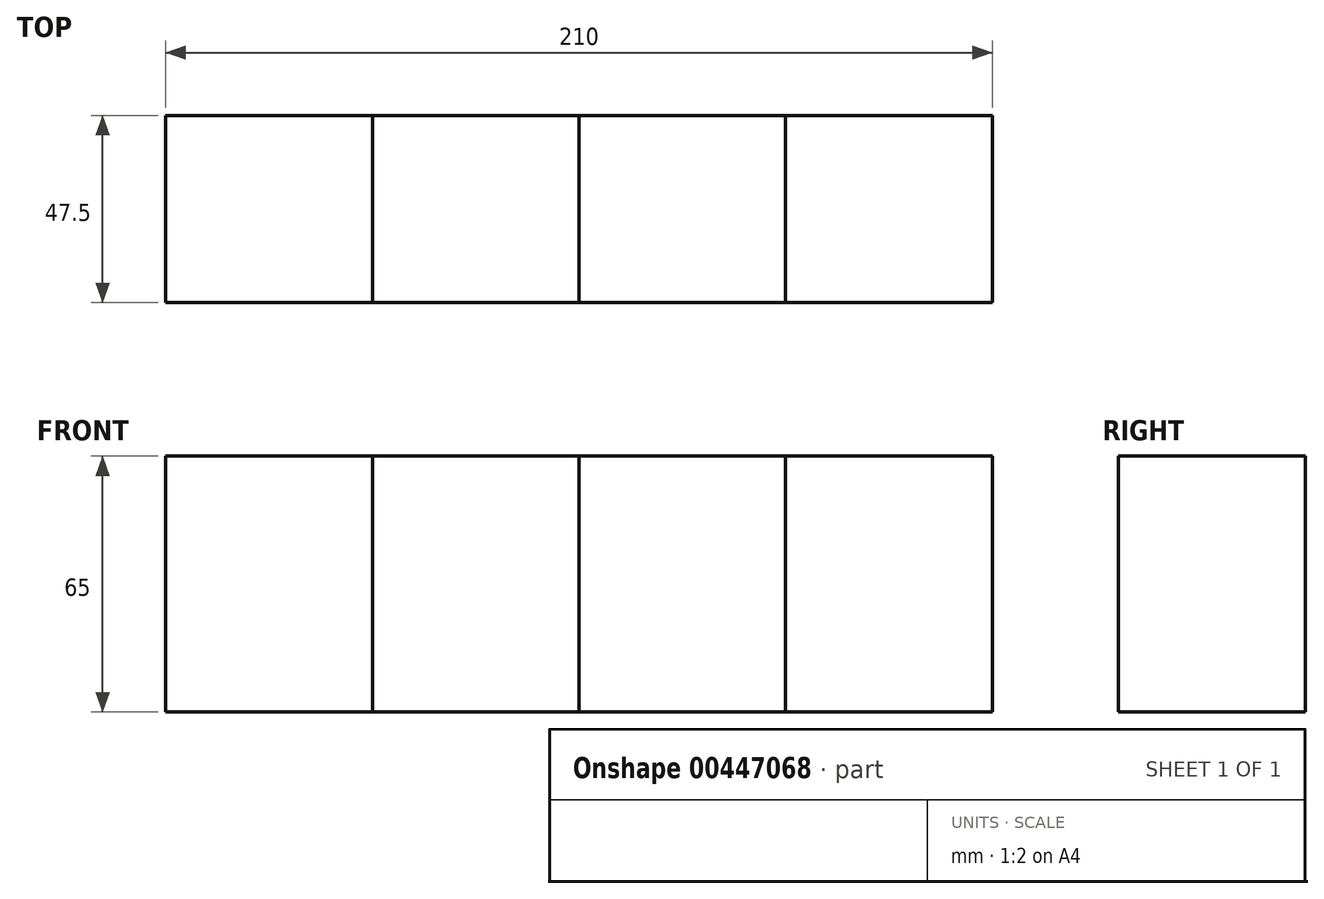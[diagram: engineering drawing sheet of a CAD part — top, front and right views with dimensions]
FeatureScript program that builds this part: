
annotation { "Feature Type Name" : "Feature", "Feature Type Description" : "" }
export const myFeature = defineFeature(function(context is Context, id is Id, definition is map)
    precondition{}
    {
        {
            var Q0;
            Q0=qCreatedBy(makeId("Right.planeOp"),FACE);
            var sketch = newSketch(context, id + "F0", { "sketchPlane" : qUnion([Q0])});
            skLineSegment(sketch, "E0.bottom", {"start": v(50, -32.5) * mm, "end": v(-50, -32.5) * mm});
            skLineSegment(sketch, "E0.top", {"start": v(50, 32.5) * mm, "end": v(-50, 32.5) * mm});
            skLineSegment(sketch, "E0.left", {"start": v(50, -32.5) * mm, "end": v(50, 32.5) * mm});
            skLineSegment(sketch, "E0.right", {"start": v(-50, -32.5) * mm, "end": v(-50, 32.5) * mm});
            skPoint(sketch, "E0.middle", {"position": v(0, 0) * mm});
            skLineSegment(sketch, "E1", {"start": v(2.5, -32.5) * mm, "end": v(2.5, 32.5) * mm});
            skSolve(sketch);
        }
        {
            var Q0;
            Q0=makeQuery(id+"F0.imprint","IMPRINT",FACE,{"disambiguationData":[TD([[makeQuery(id+"F0.imprint","IMPRINT",EDGE,{"derivedFrom":sQuery(id+"F0.wireOp",EDGE,"E0.bottom")}),-1.0]])]});
            extrude(context, id + "F1", {"entities" : qUnion([Q0]), "depth" : 210 * mm});
        }
        {
            var Q0;
            Q0=makeQuery(id+"F0.imprint","IMPRINT",FACE,{"disambiguationData":[TD([[makeQuery(id+"F0.imprint","IMPRINT",EDGE,{"derivedFrom":sQuery(id+"F0.wireOp",EDGE,"E0.bottom")}),-1.0]])]});
            extrude(context, id + "F2", {"entities" : qUnion([Q0]), "depth" : (210 / 2) * mm});
        }
        {
            var Q0;
            Q0=makeQuery(id+"F0.imprint","IMPRINT",FACE,{"disambiguationData":[TD([[makeQuery(id+"F0.imprint","IMPRINT",EDGE,{"derivedFrom":sQuery(id+"F0.wireOp",EDGE,"E0.bottom")}),-1.0]])]});
            extrude(context, id + "F3", {"entities" : qUnion([Q0]), "depth" : (210 / 4 * 3) * mm});
        }
        {
            var Q0;
            Q0=makeQuery(id+"F0.imprint","IMPRINT",FACE,{"disambiguationData":[TD([[makeQuery(id+"F0.imprint","IMPRINT",EDGE,{"derivedFrom":sQuery(id+"F0.wireOp",EDGE,"E0.bottom")}),-1.0]])]});
            extrude(context, id + "F4", {"entities" : qUnion([Q0]), "depth" : (210 / 4) * mm, "offsetDistance" : 25 * mm});
        }
        {
            var Q0;
            Q0=makeQuery(id+"F0.imprint","IMPRINT",FACE,{"disambiguationData":[TD([[makeQuery(id+"F0.imprint","IMPRINT",EDGE,{"derivedFrom":sQuery(id+"F0.wireOp",EDGE,"E0.bottom")}),-1.0]])]});
            extrude(context, id + "F5", {"entities" : qUnion([Q0]), "depth" : 210 * mm, "offsetDistance" : 25 * mm});
        }
        {
            var Q0;
            Q0=makeQuery(id+"F5.opExtrude","SWEPT_FACE",FACE,{"disambiguationData":[OSD([sQuery(id+"F0.wireOp",EDGE,"E0.top")])]});
            var sketch = newSketch(context, id + "F6", { "sketchPlane" : qUnion([Q0])});
            skLineSegment(sketch, "E2", {"start": v(105, -50) * mm, "end": v(105, 2.5) * mm});
            skLineSegment(sketch, "E3", {"start": v(105, 2.5) * mm, "end": v(210, 2.5) * mm});
            skSolve(sketch);
        }
        {
            var Q0;
            {var subQ0=sQuery(id+"F6.wireOp",EDGE,"E2");Q0=makeQuery(id+"F6.imprint","IMPRINT",FACE,{"disambiguationData":[TD([[makeQuery(id+"F6.imprint","IMPRINT",EDGE,{"derivedFrom":subQ0}),-1.0]])]});}
            extrude(context, id + "F7", {"entities" : qUnion([Q0]), "operationType" : NewBodyOperationType.REMOVE, "endBound" : BoundingType.THROUGH_ALL, "oppositeDirection" : true, "depth" : 25 * mm, "offsetDistance" : 25 * mm});
        }
        {
            var Q0;
            Q0=makeQuery(id+"F0.imprint","IMPRINT",FACE,{"disambiguationData":[TD([[makeQuery(id+"F0.imprint","IMPRINT",EDGE,{"derivedFrom":sQuery(id+"F0.wireOp",EDGE,"E0.bottom")}),-1.0]])]});
            extrude(context, id + "F8", {"entities" : qUnion([Q0]), "depth" : 105 * mm, "offsetDistance" : 25 * mm});
        }
        {
            var Q0;
            Q0=makeQuery(id+"F8.opExtrude","SWEPT_FACE",FACE,{"disambiguationData":[OSD([sQuery(id+"F0.wireOp",EDGE,"E0.top")])]});
            var sketch = newSketch(context, id + "F9", { "sketchPlane" : qUnion([Q0])});
            skLineSegment(sketch, "E4", {"start": v(0, 2.5) * mm, "end": v(105, 2.5) * mm});
            skSolve(sketch);
        }
        {
            var Q0;
            {var subQ0=sQuery(id+"F9.wireOp",EDGE,"E4");Q0=makeQuery(id+"F9.imprint","IMPRINT",FACE,{"disambiguationData":[TD([[makeQuery(id+"F9.imprint","IMPRINT",EDGE,{"derivedFrom":subQ0}),-1.0]])]});}
            extrude(context, id + "F10", {"entities" : qUnion([Q0]), "operationType" : NewBodyOperationType.REMOVE, "endBound" : BoundingType.THROUGH_ALL, "oppositeDirection" : true, "depth" : 25 * mm, "offsetDistance" : 25 * mm});
        }
        {
            var Q0;
            {var subQ0=sQuery(id+"F0.wireOp",EDGE,"E0.left");Q0=makeQuery(id+"F0.imprint","IMPRINT",FACE,{"disambiguationData":[TD([[makeQuery(id+"F0.imprint","IMPRINT",EDGE,{"derivedFrom":subQ0}),1.0]])]});}
            extrude(context, id + "F11", {"entities" : qUnion([Q0]), "depth" : 210 * mm, "offsetDistance" : 25 * mm});
        }
        {
            var Q0;
            {var subQ0=sQuery(id+"F0.wireOp",EDGE,"E0.left");Q0=makeQuery(id+"F0.imprint","IMPRINT",FACE,{"disambiguationData":[TD([[makeQuery(id+"F0.imprint","IMPRINT",EDGE,{"derivedFrom":subQ0}),1.0]])]});}
            extrude(context, id + "F12", {"entities" : qUnion([Q0]), "depth" : (210 / 4 * 3) * mm, "offsetDistance" : 25 * mm});
        }
        {
            var Q0;
            {var subQ0=sQuery(id+"F0.wireOp",EDGE,"E0.left");Q0=makeQuery(id+"F0.imprint","IMPRINT",FACE,{"disambiguationData":[TD([[makeQuery(id+"F0.imprint","IMPRINT",EDGE,{"derivedFrom":subQ0}),1.0]])]});}
            extrude(context, id + "F13", {"entities" : qUnion([Q0]), "depth" : 210 * mm, "offsetDistance" : 25 * mm});
        }
    });
